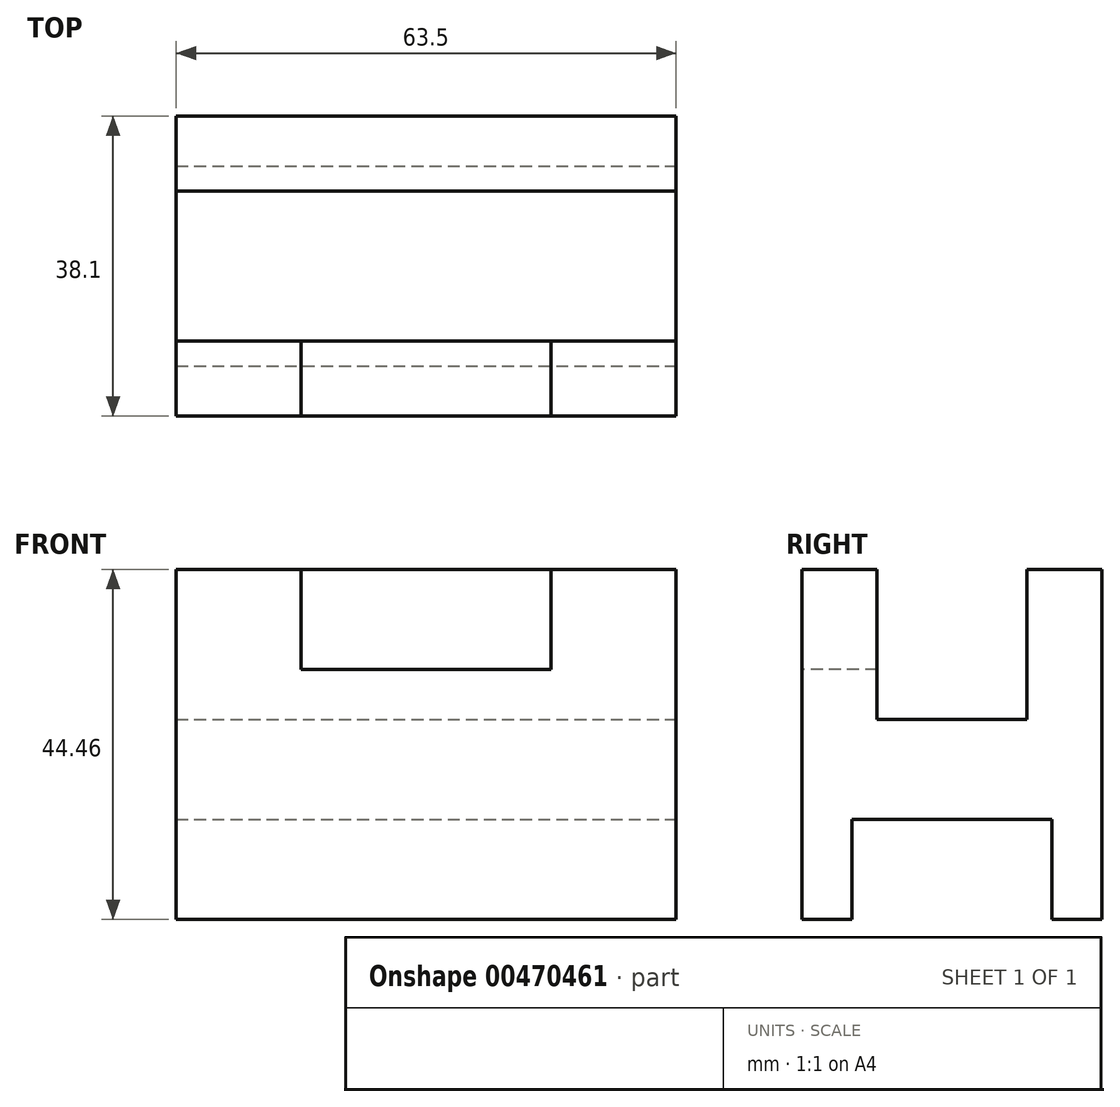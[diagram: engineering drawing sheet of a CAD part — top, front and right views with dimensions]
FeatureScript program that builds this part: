
annotation { "Feature Type Name" : "Feature", "Feature Type Description" : "" }
export const myFeature = defineFeature(function(context is Context, id is Id, definition is map)
    precondition{}
    {
        {
            var Q0;
            Q0=qCreatedBy(makeId("Front.planeOp"),FACE);
            var sketch = newSketch(context, id + "F0", { "sketchPlane" : qUnion([Q0])});
            skLineSegment(sketch, "E0.bottom", {"start": v(31.75, 22.23) * mm, "end": v(-31.75, 22.23) * mm});
            skLineSegment(sketch, "E0.top", {"start": v(31.75, -22.23) * mm, "end": v(-31.75, -22.23) * mm});
            skLineSegment(sketch, "E0.left", {"start": v(31.75, 22.23) * mm, "end": v(31.75, -22.23) * mm});
            skLineSegment(sketch, "E0.right", {"start": v(-31.75, 22.23) * mm, "end": v(-31.75, -22.23) * mm});
            skPoint(sketch, "E0.middle", {"position": v(0, 0) * mm});
            skSolve(sketch);
        }
        {
            var Q0;
            Q0 = qSketchRegion(id + "F0", true);
            var Q1;
            Q1 = qSketchRegion(id + "F2", true);
            extrude(context, id + "F1", {"entities" : qUnion([Q0, Q1]), "depth" : 38.1 * mm});
        }
        {
            var Q0;
            Q0=makeQuery(id+"F1.opExtrude","SWEPT_FACE",FACE,{"disambiguationData":[OSD([sQuery(id+"F0.wireOp",EDGE,"E0.left")])]});
            var sketch = newSketch(context, id + "F2", { "sketchPlane" : qUnion([Q0])});
            skLineSegment(sketch, "E1.bottom", {"start": v(-28.57, 22.23) * mm, "end": v(-9.52, 22.23) * mm});
            skLineSegment(sketch, "E1.top", {"start": v(-28.58, 3.17) * mm, "end": v(-9.52, 3.17) * mm});
            skLineSegment(sketch, "E1.left", {"start": v(-28.58, 22.23) * mm, "end": v(-28.58, 3.17) * mm});
            skLineSegment(sketch, "E1.right", {"start": v(-9.52, 22.23) * mm, "end": v(-9.52, 3.17) * mm});
            skSolve(sketch);
        }
        {
            var Q0;
            Q0=makeQuery(id+"F2.imprint","IMPRINT",FACE,{"disambiguationData":[TD([[makeQuery(id+"F2.imprint","IMPRINT",EDGE,{"derivedFrom":sQuery(id+"F2.wireOp",EDGE,"E1.bottom")}),-1.0]])]});
            extrude(context, id + "F3", {"entities" : qUnion([Q0]), "operationType" : NewBodyOperationType.REMOVE, "endBound" : BoundingType.THROUGH_ALL, "oppositeDirection" : true, "depth" : 25.4 * mm});
        }
        {
            var Q0;
            Q0=makeQuery(id+"F1.opExtrude","CAP_FACE",FACE,{"disambiguationData":[OSD([sQuery(id+"F0.wireOp",EDGE,"E0.bottom"),sQuery(id+"F0.wireOp",EDGE,"E0.top"),sQuery(id+"F0.wireOp",EDGE,"E0.left"),sQuery(id+"F0.wireOp",EDGE,"E0.right")])],"isStart":false});
            var sketch = newSketch(context, id + "F4", { "sketchPlane" : qUnion([Q0])});
            skLineSegment(sketch, "E2.bottom", {"start": v(-15.87, 22.23) * mm, "end": v(15.87, 22.23) * mm});
            skLineSegment(sketch, "E2.top", {"start": v(-15.88, 9.53) * mm, "end": v(15.87, 9.53) * mm});
            skLineSegment(sketch, "E2.left", {"start": v(-15.88, 22.23) * mm, "end": v(-15.88, 9.53) * mm});
            skLineSegment(sketch, "E2.right", {"start": v(15.88, 22.23) * mm, "end": v(15.88, 9.53) * mm});
            skSolve(sketch);
        }
        {
            var Q0;
            Q0 = qSketchRegion(id + "F4", true);
            extrude(context, id + "F5", {"entities" : qUnion([Q0]), "operationType" : NewBodyOperationType.REMOVE, "oppositeDirection" : true, "depth" : 25.4 * mm});
        }
        {
            var Q0;
            Q0=makeQuery(id+"F1.opExtrude","SWEPT_FACE",FACE,{"disambiguationData":[OSD([sQuery(id+"F0.wireOp",EDGE,"E0.left")])]});
            var sketch = newSketch(context, id + "F6", { "sketchPlane" : qUnion([Q0])});
            skLineSegment(sketch, "E3.bottom", {"start": v(-31.75, -22.23) * mm, "end": v(-6.35, -22.23) * mm});
            skLineSegment(sketch, "E3.top", {"start": v(-31.75, -9.53) * mm, "end": v(-6.35, -9.53) * mm});
            skLineSegment(sketch, "E3.left", {"start": v(-31.75, -22.23) * mm, "end": v(-31.75, -9.53) * mm});
            skLineSegment(sketch, "E3.right", {"start": v(-6.35, -22.23) * mm, "end": v(-6.35, -9.53) * mm});
            skSolve(sketch);
        }
        {
            var Q0;
            Q0=makeQuery(id+"F6.imprint","IMPRINT",FACE,{"disambiguationData":[TD([[makeQuery(id+"F6.imprint","IMPRINT",EDGE,{"derivedFrom":sQuery(id+"F6.wireOp",EDGE,"E3.bottom")}),1.0]])]});
            extrude(context, id + "F7", {"entities" : qUnion([Q0]), "operationType" : NewBodyOperationType.REMOVE, "endBound" : BoundingType.THROUGH_ALL, "oppositeDirection" : true, "depth" : 25.4 * mm});
        }
    });
